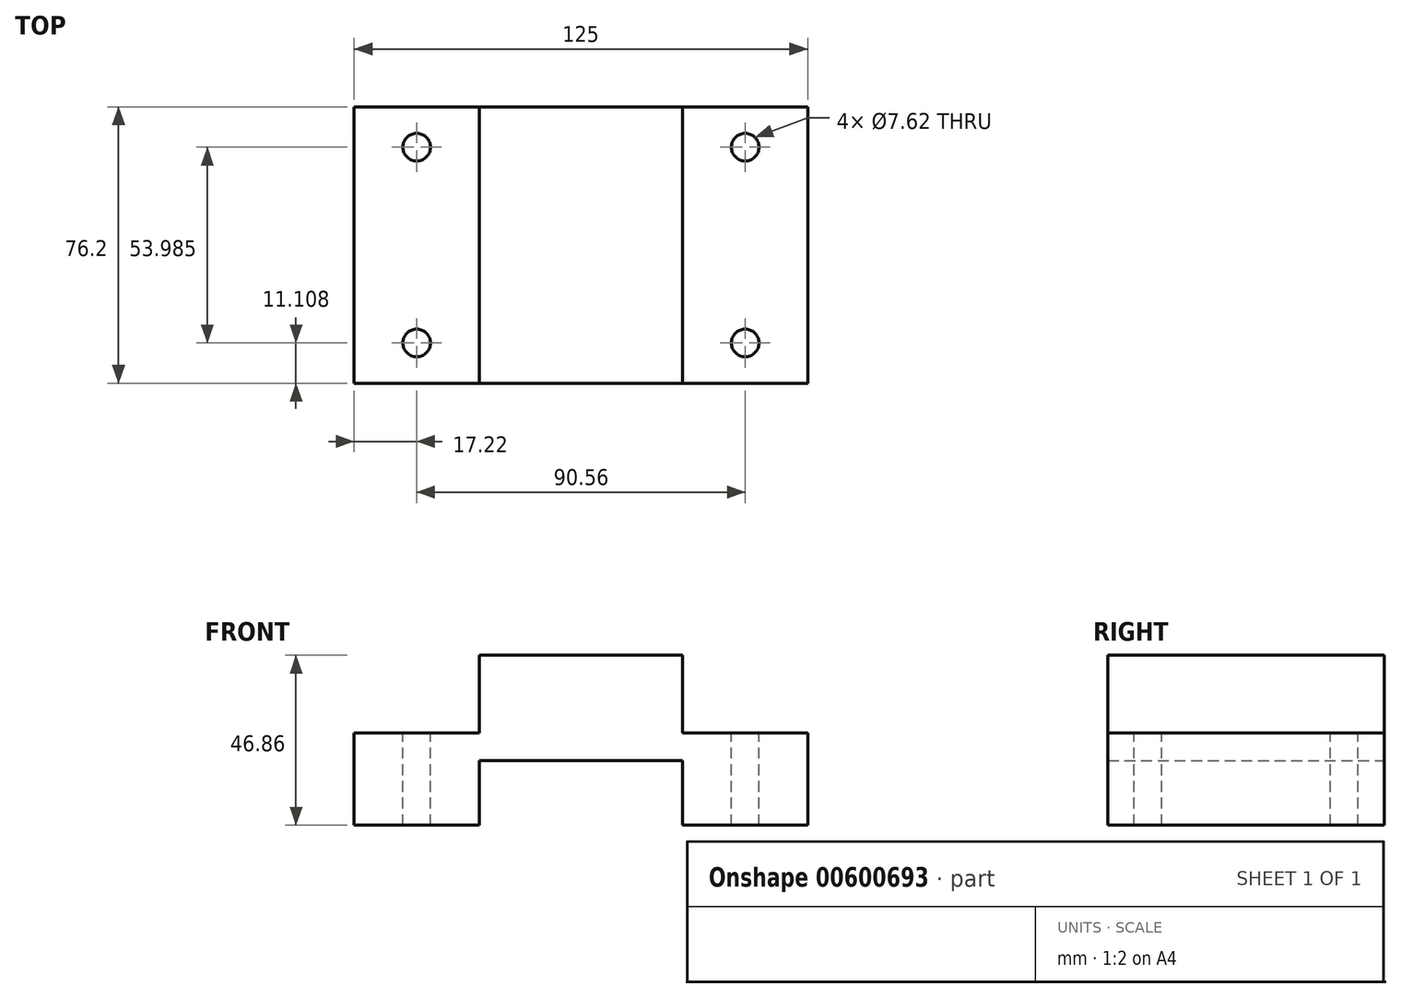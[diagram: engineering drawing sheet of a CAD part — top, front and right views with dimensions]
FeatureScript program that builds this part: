
annotation { "Feature Type Name" : "Feature", "Feature Type Description" : "" }
export const myFeature = defineFeature(function(context is Context, id is Id, definition is map)
    precondition{}
    {
        {
            var Q0;
            Q0=qCreatedBy(makeId("Front.planeOp"),FACE);
            var sketch = newSketch(context, id + "F0", { "sketchPlane" : qUnion([Q0])});
            skLineSegment(sketch, "E0", {"start": v(-28.05, 0) * mm, "end": v(-62.5, 0) * mm});
            skLineSegment(sketch, "E1", {"start": v(-62.5, 0) * mm, "end": v(-62.5, 25.4) * mm});
            skLineSegment(sketch, "E2", {"start": v(-62.5, 25.4) * mm, "end": v(-28.05, 25.4) * mm});
            skLineSegment(sketch, "E3", {"start": v(-28.05, 25.4) * mm, "end": v(-28.05, 46.86) * mm});
            skLineSegment(sketch, "E4", {"start": v(-28.05, 46.86) * mm, "end": v(0, 46.86) * mm});
            skLineSegment(sketch, "E5", {"start": v(0, 46.86) * mm, "end": v(0, 0) * mm, "construction": true});
            skLineSegment(sketch, "E6.MirrorCS", {"start": v(28.05, 46.86) * mm, "end": v(0, 46.86) * mm});
            skLineSegment(sketch, "E7.MirrorCS", {"start": v(28.05, 25.4) * mm, "end": v(28.05, 46.86) * mm});
            skLineSegment(sketch, "E8.MirrorCS", {"start": v(62.5, 25.4) * mm, "end": v(28.05, 25.4) * mm});
            skLineSegment(sketch, "E9.MirrorCS", {"start": v(62.5, 0) * mm, "end": v(62.5, 25.4) * mm});
            skLineSegment(sketch, "E10.MirrorCS", {"start": v(28.05, 0) * mm, "end": v(62.5, 0) * mm});
            skLineSegment(sketch, "E11", {"start": v(-28.05, 0) * mm, "end": v(-28.05, 17.78) * mm});
            skLineSegment(sketch, "E12", {"start": v(-28.05, 17.78) * mm, "end": v(28.05, 17.78) * mm});
            skLineSegment(sketch, "E13", {"start": v(28.05, 17.78) * mm, "end": v(28.05, 0) * mm});
            skPoint(sketch, "E14.orphan", {"position": v(0, 0) * mm});
            skSolve(sketch);
        }
        {
            var Q0;
            Q0=makeQuery(id+"F0.imprint","IMPRINT",FACE,{"disambiguationData":[TD([[makeQuery(id+"F0.imprint","IMPRINT",EDGE,{"derivedFrom":sQuery(id+"F0.wireOp",EDGE,"E0")}),-1.0]])]});
            extrude(context, id + "F1", {"entities" : qUnion([Q0]), "depth" : 76.2 * mm, "offsetDistance" : 25.4 * mm});
        }
        {
            var Q0;
            Q0=makeQuery(id+"F1.opExtrude","SWEPT_FACE",FACE,{"disambiguationData":[OSD([sQuery(id+"F0.wireOp",EDGE,"E2")])]});
            var sketch = newSketch(context, id + "F2", { "sketchPlane" : qUnion([Q0])});
            skLineSegment(sketch, "E15", {"start": v(-62.5, -38.1) * mm, "end": v(-28.05, -38.1) * mm, "construction": true});
            skLineSegment(sketch, "E16", {"start": v(-45.28, 0) * mm, "end": v(-45.28, -76.2) * mm, "construction": true});
            skLineSegment(sketch, "E17", {"start": v(-28.05, -11.1) * mm, "end": v(-45.28, -11.1) * mm, "construction": true});
            skLineSegment(sketch, "E18.MirrorCS", {"start": v(-28.05, -65.1) * mm, "end": v(-45.28, -65.1) * mm, "construction": true});
            skSolve(sketch);
        }
        {
            var Q0;
            Q0=sQuery(id+"F2.wireOp",VERTEX,"E17.end");
            var Q1;
            Q1=sQuery(id+"F2.wireOp",VERTEX,"E18.MirrorCS.end");
            var Q2;
            Q2=makeQuery(id+"F1.opExtrude","SWEPT_BODY",BODY,{"disambiguationData":[OSD([sQuery(id+"F0.wireOp",EDGE,"E0"),sQuery(id+"F0.wireOp",EDGE,"E1"),sQuery(id+"F0.wireOp",EDGE,"E2"),sQuery(id+"F0.wireOp",EDGE,"E3"),sQuery(id+"F0.wireOp",EDGE,"E4"),sQuery(id+"F0.wireOp",EDGE,"E6.MirrorCS"),sQuery(id+"F0.wireOp",EDGE,"E7.MirrorCS"),sQuery(id+"F0.wireOp",EDGE,"E8.MirrorCS"),sQuery(id+"F0.wireOp",EDGE,"E9.MirrorCS"),sQuery(id+"F0.wireOp",EDGE,"E10.MirrorCS"),sQuery(id+"F0.wireOp",EDGE,"E11"),sQuery(id+"F0.wireOp",EDGE,"E12"),sQuery(id+"F0.wireOp",EDGE,"E13")])]});
            hole(context, id + "F3", {"style" : HoleStyle.SIMPLE, "endStyle" : HoleEndStyle.THROUGH, "holeDiameter" : 7.62 * mm, "majorDiameter" : 6.35 * mm, "isTappedThrough" : true, "tappedDepth" : 12.7 * mm, "tapClearance" : 3, "locations" : qUnion([Q0, Q1]), "scope" : qUnion([Q2])});
        }
        {
            var Q0;
            Q0=makeQuery(id+"F1.opExtrude","SWEPT_FACE",FACE,{"disambiguationData":[OSD([sQuery(id+"F0.wireOp",EDGE,"E8.MirrorCS")])]});
            var sketch = newSketch(context, id + "F4", { "sketchPlane" : qUnion([Q0])});
            skLineSegment(sketch, "E19", {"start": v(45.28, 0) * mm, "end": v(45.28, -76.2) * mm, "construction": true});
            skLineSegment(sketch, "E20.0.0", {"start": v(-28.05, 0) * mm, "end": v(-62.5, 0) * mm, "construction": true});
            skLineSegment(sketch, "E20.0.1", {"start": v(-62.5, 0) * mm, "end": v(-62.5, -76.2) * mm, "construction": true});
            skLineSegment(sketch, "E20.0.2", {"start": v(-62.5, -76.2) * mm, "end": v(-28.05, -76.2) * mm, "construction": true});
            skLineSegment(sketch, "E20.0.3", {"start": v(-28.05, -76.2) * mm, "end": v(-28.05, 0) * mm, "construction": true});
            skCircle(sketch, "E21.0", {"center": v(-45.28, -11.1) * mm, "radius": 3.8 * mm, "construction": true});
            skCircle(sketch, "E22.0", {"center": v(-45.28, -65.1) * mm, "radius": 3.8 * mm, "construction": true});
            skLineSegment(sketch, "E23", {"start": v(-45.28, -11.1) * mm, "end": v(45.28, -11.1) * mm, "construction": true});
            skLineSegment(sketch, "E24", {"start": v(-45.28, -65.1) * mm, "end": v(45.28, -65.1) * mm, "construction": true});
            skSolve(sketch);
        }
        {
            var Q0;
            Q0=sQuery(id+"F4.wireOp",VERTEX,"E23.end");
            var Q1;
            Q1=sQuery(id+"F4.wireOp",VERTEX,"E24.end");
            var Q2;
            Q2=makeQuery(id+"F1.opExtrude","SWEPT_BODY",BODY,{"disambiguationData":[OSD([sQuery(id+"F0.wireOp",EDGE,"E0"),sQuery(id+"F0.wireOp",EDGE,"E1"),sQuery(id+"F0.wireOp",EDGE,"E2"),sQuery(id+"F0.wireOp",EDGE,"E3"),sQuery(id+"F0.wireOp",EDGE,"E4"),sQuery(id+"F0.wireOp",EDGE,"E6.MirrorCS"),sQuery(id+"F0.wireOp",EDGE,"E7.MirrorCS"),sQuery(id+"F0.wireOp",EDGE,"E8.MirrorCS"),sQuery(id+"F0.wireOp",EDGE,"E9.MirrorCS"),sQuery(id+"F0.wireOp",EDGE,"E10.MirrorCS"),sQuery(id+"F0.wireOp",EDGE,"E11"),sQuery(id+"F0.wireOp",EDGE,"E12"),sQuery(id+"F0.wireOp",EDGE,"E13")])]});
            hole(context, id + "F5", {"style" : HoleStyle.SIMPLE, "endStyle" : HoleEndStyle.THROUGH, "holeDiameter" : 7.62 * mm, "majorDiameter" : 6.35 * mm, "isTappedThrough" : true, "tappedDepth" : 12.7 * mm, "tapClearance" : 3, "locations" : qUnion([Q0, Q1]), "scope" : qUnion([Q2])});
        }
    });
